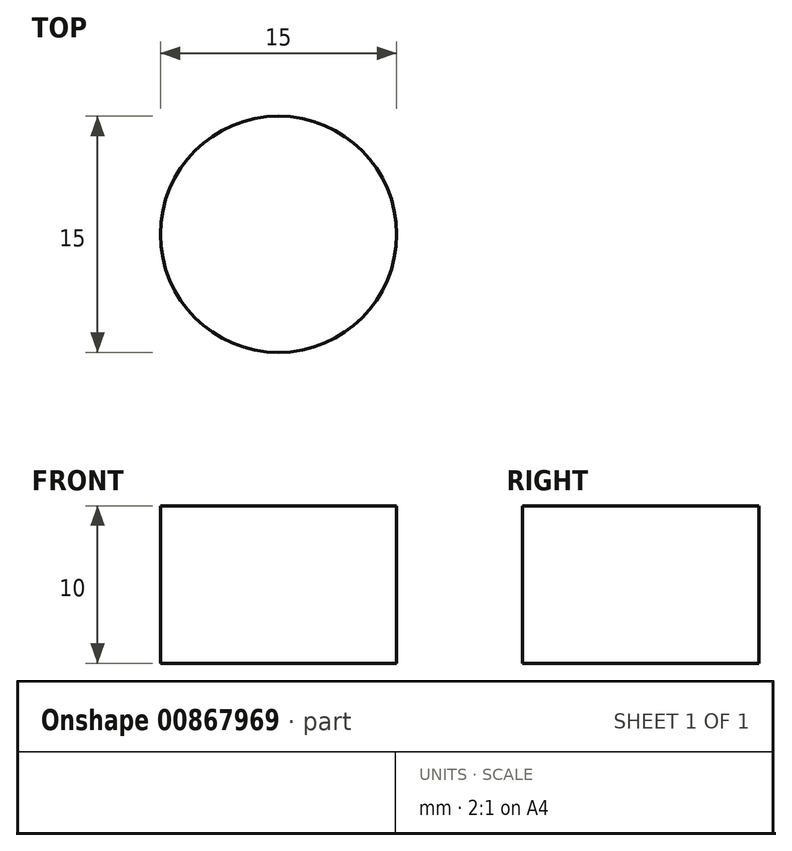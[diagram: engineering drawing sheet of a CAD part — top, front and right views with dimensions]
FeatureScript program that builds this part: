
annotation { "Feature Type Name" : "Feature", "Feature Type Description" : "" }
export const myFeature = defineFeature(function(context is Context, id is Id, definition is map)
    precondition{}
    {
        {
            var Q0;
            Q0=qCreatedBy(makeId("Top.planeOp"),FACE);
            var sketch = newSketch(context, id + "F0", { "sketchPlane" : qUnion([Q0])});
            skCircle(sketch, "E0", {"center": v(0, 0) * mm, "radius": 7.5 * mm});
            skSolve(sketch);
        }
        {
            var Q0;
            Q0=makeQuery(id+"F0.imprint","IMPRINT",FACE,{"disambiguationData":[TD([[makeQuery(id+"F0.imprint","IMPRINT",EDGE,{"derivedFrom":sQuery(id+"F0.wireOp",EDGE,"E0")}),1.0]])]});
            extrude(context, id + "F1", {"entities" : qUnion([Q0]), "depth" : 10 * mm, "offsetDistance" : 25 * mm});
        }
    });
